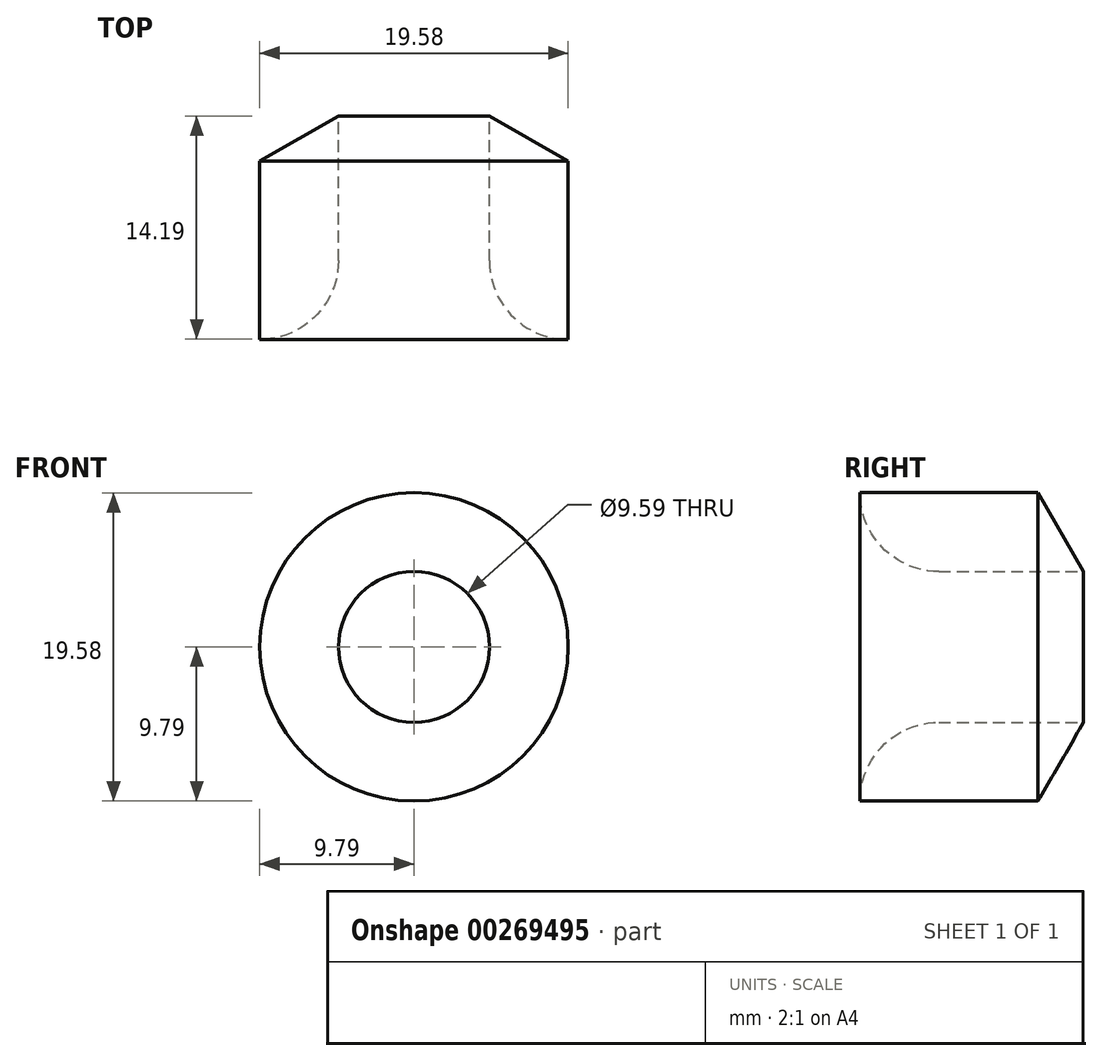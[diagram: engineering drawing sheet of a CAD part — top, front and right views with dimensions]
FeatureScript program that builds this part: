
annotation { "Feature Type Name" : "Feature", "Feature Type Description" : "" }
export const myFeature = defineFeature(function(context is Context, id is Id, definition is map)
    precondition{}
    {
        {
            var Q0;
            Q0=qCreatedBy(makeId("Top.planeOp"),FACE);
            var sketch = newSketch(context, id + "F0", { "sketchPlane" : qUnion([Q0])});
            skCircle(sketch, "E0.cCircle", {"center": v(0, 0) * mm, "radius": 11.3 * mm, "construction": true});
            skLineSegment(sketch, "E0.0", {"start": v(0, -11.3) * mm, "end": v(-9.8, -5.65) * mm});
            skLineSegment(sketch, "E0.1", {"start": v(-9.8, -5.65) * mm, "end": v(-9.8, 5.65) * mm});
            skLineSegment(sketch, "E0.2", {"start": v(-9.8, 5.65) * mm, "end": v(0, 11.3) * mm});
            skLineSegment(sketch, "E0.3", {"start": v(0, 11.3) * mm, "end": v(9.8, 5.65) * mm});
            skLineSegment(sketch, "E0.4", {"start": v(9.8, 5.65) * mm, "end": v(9.8, -5.65) * mm});
            skLineSegment(sketch, "E0.5", {"start": v(9.8, -5.65) * mm, "end": v(0, -11.3) * mm});
            skLineSegment(sketch, "E1", {"start": v(0, 11.3) * mm, "end": v(0, -11.3) * mm});
            skSolve(sketch);
        }
        {
            var Q0;
            Q0=makeQuery(id+"F0.imprint","IMPRINT",FACE,{"disambiguationData":[TD([[makeQuery(id+"F0.imprint","IMPRINT",EDGE,{"derivedFrom":sQuery(id+"F0.wireOp",EDGE,"E0.3")}),-1.0]])]});
            var Q1;
            Q1=sQuery(id+"F0.wireOp",EDGE,"E1");
            revolve(context, id + "F1", {"entities" : qUnion([Q0]), "axis" : qUnion([Q1]), "revolveType" : RevolveType.FULL});
        }
        {
            var Q0;
            Q0=makeQuery(id+"F1.opRevolve","SWEPT_FACE",FACE,{"disambiguationData":[OSD([sQuery(id+"F0.wireOp",EDGE,"E0.5")])]});
            var Q1;
            Q1=makeQuery(id+"F1.opRevolve","SWEPT_FACE",FACE,{"disambiguationData":[OSD([sQuery(id+"F0.wireOp",EDGE,"E0.3")])]});
            shell(context, id + "F2", {"entities" : qUnion([Q0, Q1]), "thickness" : 5 * mm});
        }
        {
            var Q0;
            Q0=makeQuery(id+"F2.opShell","OFFSET_EDGE",EDGE,{"disambiguationData":[OSD([sQuery(id+"F0.wireOp",EDGE,"E0.4"),sQuery(id+"F0.wireOp",EDGE,"E0.5")])]});
            fillet(context, id + "F3", {"entities" : qUnion([Q0]), "radius" : 5 * mm, "tangentPropagation" : true, "allowEdgeOverflow" : false});
        }
    });
